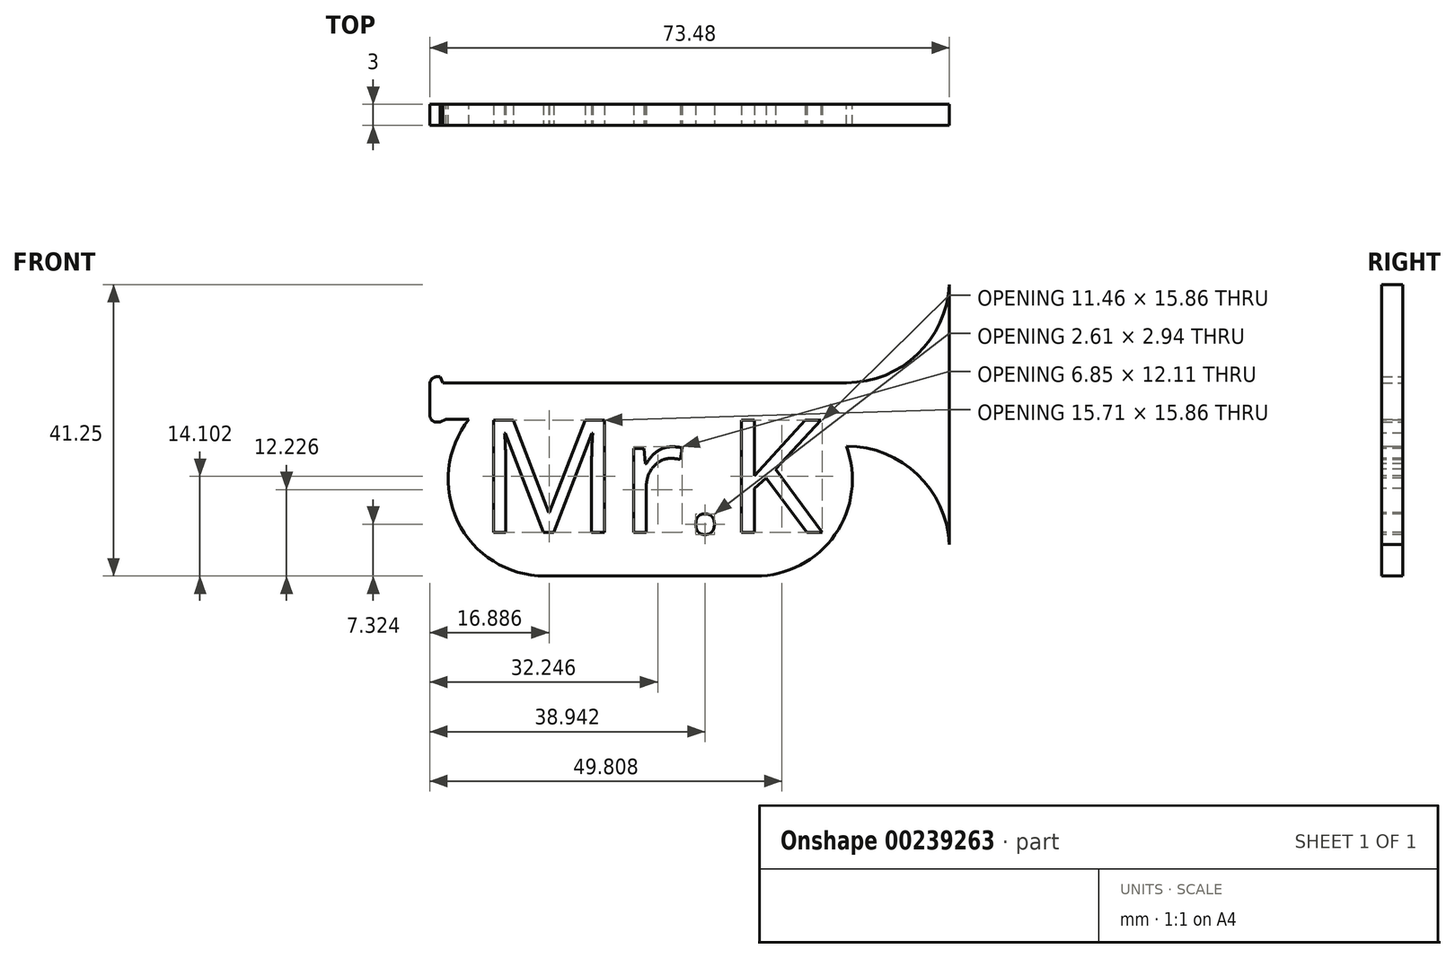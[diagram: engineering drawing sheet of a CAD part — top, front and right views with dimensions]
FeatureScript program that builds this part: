
annotation { "Feature Type Name" : "Feature", "Feature Type Description" : "" }
export const myFeature = defineFeature(function(context is Context, id is Id, definition is map)
    precondition{}
    {
        {
            var Q0;
            Q0=qCreatedBy(makeId("Front.planeOp"),FACE);
            var sketch = newSketch(context, id + "F0", { "sketchPlane" : qUnion([Q0])});
            skArc(sketch, "E0", {"start": v(-10.7, 8.5) * mm, "mid": v(-12.3, -5.95) * mm, "end": v(0, -13.67) * mm});
            skArc(sketch, "E1", {"start": v(29.83, -13.67) * mm, "mid": v(41.04, -7.82) * mm, "end": v(42.66, 4.72) * mm});
            skLineSegment(sketch, "E2", {"start": v(0, 13.67) * mm, "end": v(29.83, 13.67) * mm});
            skLineSegment(sketch, "E3", {"start": v(0, -13.67) * mm, "end": v(29.83, -13.67) * mm});
            skLineSegment(sketch, "E4", {"start": v(0, 13.67) * mm, "end": v(-14.43, 13.67) * mm});
            skLineSegment(sketch, "E5", {"start": v(-14.43, 13.67) * mm, "end": v(-14.83, 14.51) * mm});
            skLineSegment(sketch, "E6", {"start": v(-14.83, 14.51) * mm, "end": v(-15.27, 14.51) * mm});
            skLineSegment(sketch, "E7", {"start": v(-16.27, 13.51) * mm, "end": v(-16.27, 9.1) * mm});
            skLineSegment(sketch, "E8", {"start": v(-15.27, 8.1) * mm, "end": v(-14.83, 8.1) * mm});
            skLineSegment(sketch, "E9", {"start": v(-14.83, 8.1) * mm, "end": v(-13.99, 8.5) * mm});
            skLineSegment(sketch, "E10", {"start": v(-13.99, 8.5) * mm, "end": v(-10.7, 8.5) * mm});
            skPoint(sketch, "E11.visualSharp", {"position": v(-16.27, 14.51) * mm});
            skArc(sketch, "E11.filletArc", {"start": v(-15.27, 14.51) * mm, "mid": v(-15.98, 14.22) * mm, "end": v(-16.27, 13.51) * mm});
            skPoint(sketch, "E12.visualSharp", {"position": v(-16.27, 8.1) * mm});
            skArc(sketch, "E12.filletArc", {"start": v(-16.27, 9.1) * mm, "mid": v(-15.98, 8.4) * mm, "end": v(-15.27, 8.1) * mm});
            skLineSegment(sketch, "E13", {"start": v(29.83, 13.67) * mm, "end": v(42.66, 13.67) * mm});
            skLineSegment(sketch, "E14", {"start": v(42.66, 4.72) * mm, "end": v(42.66, 4.72) * mm});
            skLineSegment(sketch, "E15", {"start": v(42.66, 13.67) * mm, "end": v(42.66, 4.72) * mm, "construction": true});
            skArc(sketch, "E16", {"start": v(42.66, 13.67) * mm, "mid": v(53.19, 18.17) * mm, "end": v(57.21, 28.88) * mm});
            skArc(sketch, "E17", {"start": v(57.21, -9.2) * mm, "mid": v(52.73, 0.68) * mm, "end": v(42.66, 4.72) * mm});
            skLineSegment(sketch, "E18", {"start": v(42.66, 28.23) * mm, "end": v(42.66, -9.84) * mm, "construction": true});
            skLineSegment(sketch, "E19", {"start": v(57.21, 28.88) * mm, "end": v(57.21, -9.2) * mm});
            skPoint(sketch, "E20.endSnap0", {"position": v(-9.18, -0.02) * mm});
            skPoint(sketch, "E21.orphan", {"position": v(-9.18, 0) * mm});
            skPoint(sketch, "E22.orphan", {"position": v(-11.92, -0.02) * mm});
            skPoint(sketch, "E23.bottom.end.orphan", {"position": v(-9.18, 5.36) * mm});
            skPoint(sketch, "E23.bottom.start.orphan", {"position": v(-11.92, 5.36) * mm});
            skPoint(sketch, "E23.top.start.orphan", {"position": v(-11.92, -5.4) * mm});
            skPoint(sketch, "E24.trimOffspring.end.orphan", {"position": v(-9.18, -5.4) * mm});
            skSolve(sketch);
        }
        {
            var Q0;
            Q0=makeQuery(id+"F0.imprint","IMPRINT",FACE,{"disambiguationData":[TD([[makeQuery(id+"F0.imprint","IMPRINT",EDGE,{"derivedFrom":sQuery(id+"F0.wireOp",EDGE,"E0")}),1.0]])]});
            extrude(context, id + "F1", {"entities" : qUnion([Q0]), "depth" : 3 * mm});
        }
        {
            var Q0;
            Q0=makeQuery(id+"F1.opExtrude","CAP_FACE",FACE,{"disambiguationData":[OSD([sQuery(id+"F0.wireOp",EDGE,"E0"),sQuery(id+"F0.wireOp",EDGE,"E1"),sQuery(id+"F0.wireOp",EDGE,"E2"),sQuery(id+"F0.wireOp",EDGE,"E3"),sQuery(id+"F0.wireOp",EDGE,"E4"),sQuery(id+"F0.wireOp",EDGE,"E5"),sQuery(id+"F0.wireOp",EDGE,"E6"),sQuery(id+"F0.wireOp",EDGE,"E7"),sQuery(id+"F0.wireOp",EDGE,"E8"),sQuery(id+"F0.wireOp",EDGE,"E9"),sQuery(id+"F0.wireOp",EDGE,"E10"),sQuery(id+"F0.wireOp",EDGE,"E11.filletArc"),sQuery(id+"F0.wireOp",EDGE,"E12.filletArc"),sQuery(id+"F0.wireOp",EDGE,"E13"),sQuery(id+"F0.wireOp",EDGE,"E16"),sQuery(id+"F0.wireOp",EDGE,"E17"),sQuery(id+"F0.wireOp",EDGE,"E19")])],"isStart":false});
            var sketch = newSketch(context, id + "F2", { "sketchPlane" : qUnion([Q0])});
            skText(sketch, "E25", { "text": "Mr.K", "fontName": "OpenSans-Regular.ttf"});
            const initialGuessF2  = {"E25": [-0.00942, -0.0075, 1, 0, 0.016]};
            skSetInitialGuess(sketch, initialGuessF2);
            skSolve(sketch);
        }
        {
            var Q0;
            Q0 = qSketchRegion(id + "F2", true);
            extrude(context, id + "F3", {"entities" : qUnion([Q0]), "operationType" : NewBodyOperationType.REMOVE, "oppositeDirection" : true, "depth" : 25 * mm});
        }
    });
